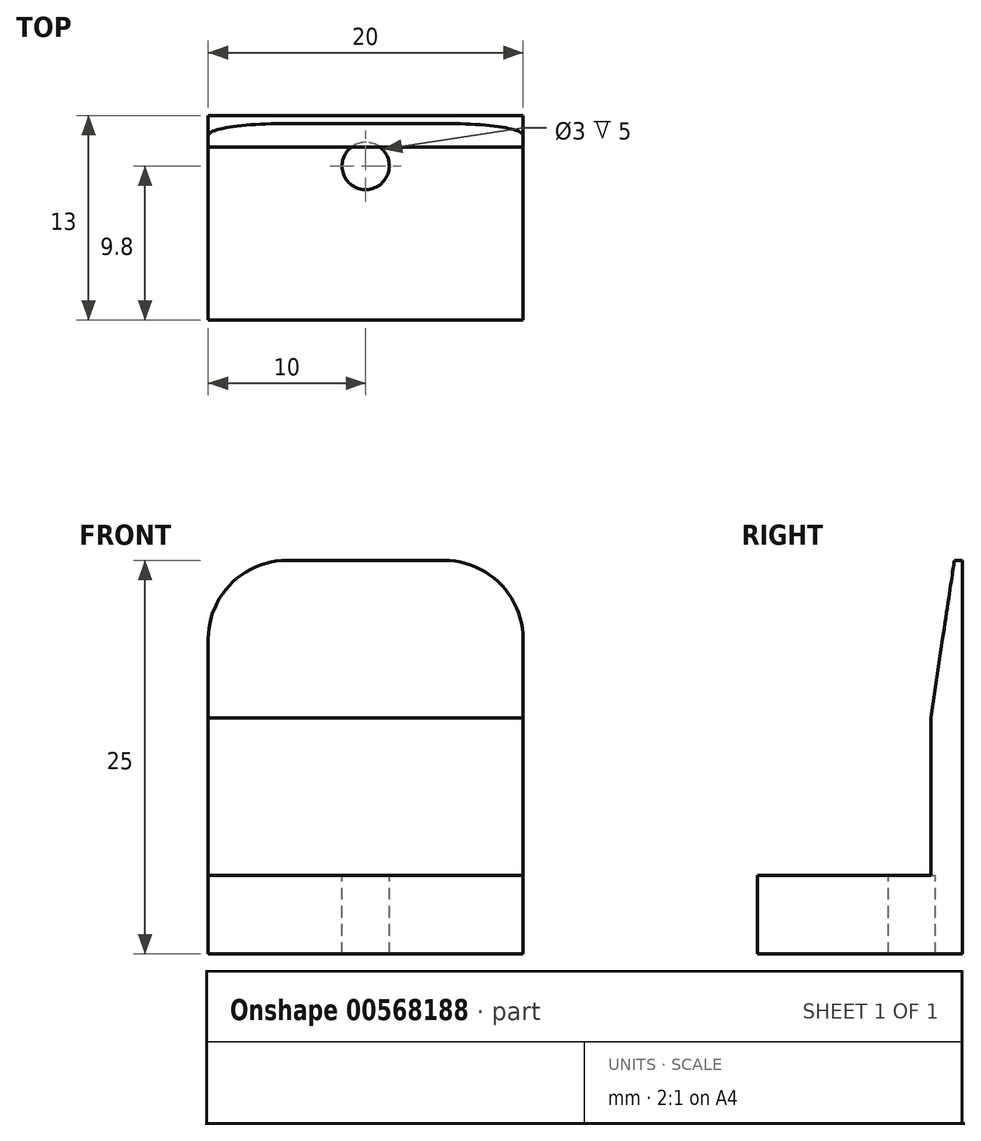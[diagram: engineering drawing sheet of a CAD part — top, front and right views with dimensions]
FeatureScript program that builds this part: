
annotation { "Feature Type Name" : "Feature", "Feature Type Description" : "" }
export const myFeature = defineFeature(function(context is Context, id is Id, definition is map)
    precondition{}
    {
        {
            var Q0;
            Q0=qCreatedBy(makeId("Top.planeOp"),FACE);
            var sketch = newSketch(context, id + "F0", { "sketchPlane" : qUnion([Q0])});
            skLineSegment(sketch, "E0.bottom", {"start": v(0, 0) * mm, "end": v(20, 0) * mm});
            skLineSegment(sketch, "E0.top", {"start": v(0, 13) * mm, "end": v(20, 13) * mm});
            skLineSegment(sketch, "E0.left", {"start": v(0, 0) * mm, "end": v(0, 13) * mm});
            skLineSegment(sketch, "E0.right", {"start": v(20, 0) * mm, "end": v(20, 13) * mm});
            skSolve(sketch);
        }
        {
            var Q0;
            Q0 = qSketchRegion(id + "F0", true);
            extrude(context, id + "F1", {"entities" : qUnion([Q0]), "depth" : 5 * mm, "offsetDistance" : 25 * mm});
        }
        {
            var Q0;
            Q0=makeQuery(id+"F1.opExtrude","CAP_FACE",FACE,{"disambiguationData":[OSD([sQuery(id+"F0.wireOp",EDGE,"E0.bottom"),sQuery(id+"F0.wireOp",EDGE,"E0.top"),sQuery(id+"F0.wireOp",EDGE,"E0.left"),sQuery(id+"F0.wireOp",EDGE,"E0.right")])],"isStart":false});
            var sketch = newSketch(context, id + "F2", { "sketchPlane" : qUnion([Q0])});
            skLineSegment(sketch, "E1.bottom", {"start": v(0, 13) * mm, "end": v(20, 13) * mm});
            skLineSegment(sketch, "E1.top", {"start": v(0, 11) * mm, "end": v(20, 11) * mm});
            skLineSegment(sketch, "E1.left", {"start": v(0, 13) * mm, "end": v(0, 11) * mm});
            skLineSegment(sketch, "E1.right", {"start": v(20, 13) * mm, "end": v(20, 11) * mm});
            skSolve(sketch);
        }
        {
            var Q0;
            Q0 = qSketchRegion(id + "F2", true);
            extrude(context, id + "F3", {"entities" : qUnion([Q0]), "operationType" : NewBodyOperationType.ADD, "depth" : 20 * mm, "offsetDistance" : 25 * mm});
        }
        {
            var Q0;
            Q0=makeQuery(id+"F3.opExtrude","CAP_EDGE",EDGE,{"disambiguationData":[OSD([sQuery(id+"F2.wireOp",EDGE,"E1.left")])],"isStart":false});
            var Q1;
            Q1=makeQuery(id+"F3.opExtrude","CAP_EDGE",EDGE,{"disambiguationData":[OSD([sQuery(id+"F2.wireOp",EDGE,"E1.right")])],"isStart":false});
            fillet(context, id + "F4", {"entities" : qUnion([Q0, Q1]), "radius" : 5 * mm, "tangentPropagation" : true, "allowEdgeOverflow" : false});
        }
        {
            var Q0;
            Q0=makeQuery(id+"F1.opExtrude","CAP_FACE",FACE,{"disambiguationData":[OSD([sQuery(id+"F0.wireOp",EDGE,"E0.bottom"),sQuery(id+"F0.wireOp",EDGE,"E0.top"),sQuery(id+"F0.wireOp",EDGE,"E0.left"),sQuery(id+"F0.wireOp",EDGE,"E0.right")])],"isStart":false});
            var sketch = newSketch(context, id + "F5", { "sketchPlane" : qUnion([Q0])});
            skLineSegment(sketch, "E2", {"start": v(10, 0) * mm, "end": v(10, 11) * mm, "construction": true});
            skCircle(sketch, "E3", {"center": v(10, 9.8) * mm, "radius": 1.5 * mm});
            skSolve(sketch);
        }
        {
            var Q0;
            Q0=makeQuery(id+"F3.boolean.opBoolean","MERGE",FACE,{"derivedFrom":[makeQuery(id+"F1.opExtrude","SWEPT_FACE",FACE,{"disambiguationData":[OSD([sQuery(id+"F0.wireOp",EDGE,"E0.left")])]}),makeQuery(id+"F3.opExtrude","SWEPT_FACE",FACE,{"disambiguationData":[OSD([sQuery(id+"F2.wireOp",EDGE,"E1.left")])]})]});
            var sketch = newSketch(context, id + "F6", { "sketchPlane" : qUnion([Q0])});
            skLineSegment(sketch, "E4", {"start": v(-12.5, 25) * mm, "end": v(-11, 15) * mm});
            skLineSegment(sketch, "E5", {"start": v(-12.5, 25) * mm, "end": v(-11, 25) * mm});
            skLineSegment(sketch, "E6", {"start": v(-11, 25) * mm, "end": v(-11, 15) * mm});
            skSolve(sketch);
        }
        {
            var Q0;
            Q0 = qSketchRegion(id + "F6", true);
            extrude(context, id + "F7", {"entities" : qUnion([Q0]), "operationType" : NewBodyOperationType.REMOVE, "oppositeDirection" : true, "depth" : 25 * mm, "offsetDistance" : 25 * mm});
        }
        {
            var Q0;
            Q0 = qSketchRegion(id + "F5", true);
            extrude(context, id + "F8", {"entities" : qUnion([Q0]), "operationType" : NewBodyOperationType.REMOVE, "oppositeDirection" : true, "depth" : 25 * mm, "offsetDistance" : 25 * mm});
        }
    });
